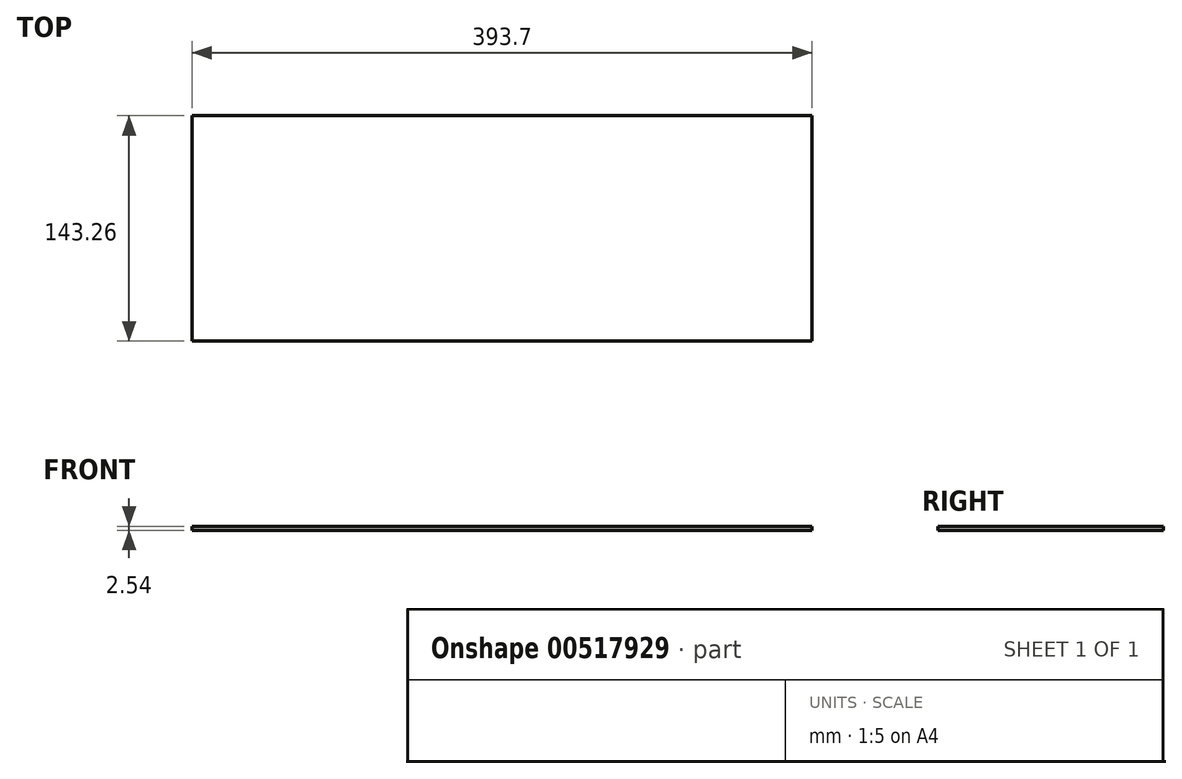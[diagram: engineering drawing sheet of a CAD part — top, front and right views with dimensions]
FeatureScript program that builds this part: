
annotation { "Feature Type Name" : "Feature", "Feature Type Description" : "" }
export const myFeature = defineFeature(function(context is Context, id is Id, definition is map)
    precondition{}
    {
        {
            var Q0;
            Q0=qCreatedBy(makeId("Front.planeOp"),FACE);
            var sketch = newSketch(context, id + "F0", { "sketchPlane" : qUnion([Q0])});
            skLineSegment(sketch, "E0", {"start": v(-183.3, 59.46) * mm, "end": v(210.4, 59.46) * mm});
            skLineSegment(sketch, "E1", {"start": v(210.4, 59.46) * mm, "end": v(210.4, 62) * mm});
            skLineSegment(sketch, "E2", {"start": v(210.4, 62) * mm, "end": v(-183.3, 62) * mm});
            skLineSegment(sketch, "E3", {"start": v(-183.3, 62) * mm, "end": v(-183.3, 59.46) * mm});
            skSolve(sketch);
        }
        {
            var Q0;
            Q0=makeQuery(id+"F0.imprint","IMPRINT",FACE,{"disambiguationData":[TD([[makeQuery(id+"F0.imprint","IMPRINT",EDGE,{"derivedFrom":sQuery(id+"F0.wireOp",EDGE,"E0")}),1.0]])]});
            extrude(context, id + "F1", {"entities" : qUnion([Q0]), "depth" : 143.26 * mm, "offsetDistance" : 25.4 * mm});
        }
    });
